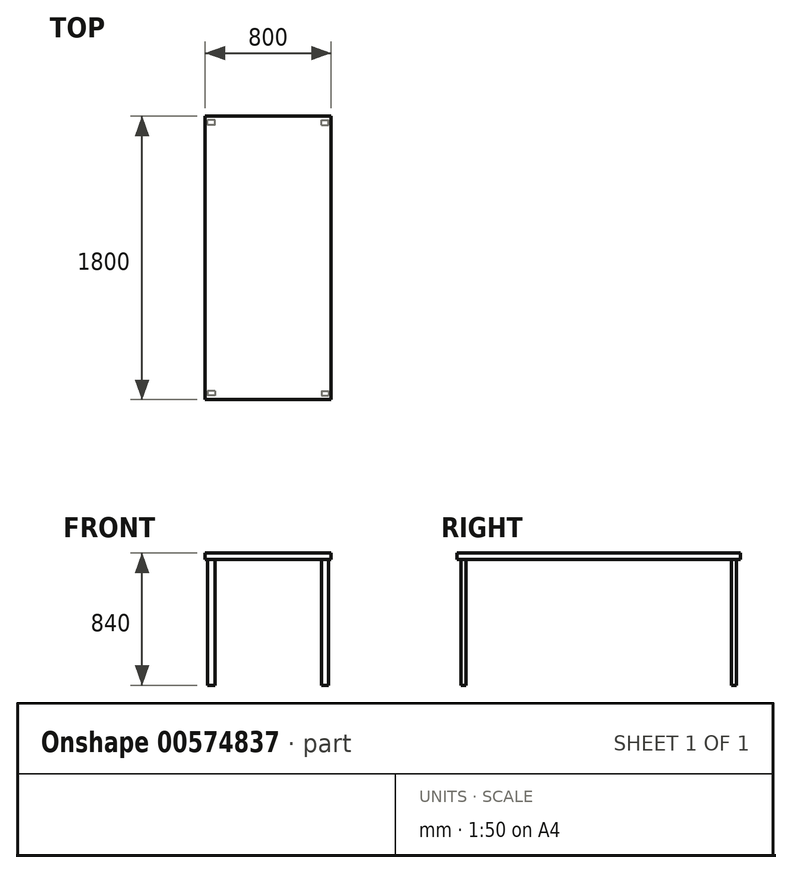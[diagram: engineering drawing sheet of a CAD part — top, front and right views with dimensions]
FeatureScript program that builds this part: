
annotation { "Feature Type Name" : "Feature", "Feature Type Description" : "" }
export const myFeature = defineFeature(function(context is Context, id is Id, definition is map)
    precondition{}
    {
        {
            var Q0;
            Q0=qCreatedBy(makeId("Front.planeOp"),FACE);
            var sketch = newSketch(context, id + "F0", { "sketchPlane" : qUnion([Q0])});
            skLineSegment(sketch, "E0.bottom", {"start": v(400, 20) * mm, "end": v(-400, 20) * mm});
            skLineSegment(sketch, "E0.top", {"start": v(400, -20) * mm, "end": v(-400, -20) * mm});
            skLineSegment(sketch, "E0.left", {"start": v(400, 20) * mm, "end": v(400, -20) * mm});
            skLineSegment(sketch, "E0.right", {"start": v(-400, 20) * mm, "end": v(-400, -20) * mm});
            skPoint(sketch, "E0.middle", {"position": v(0, 0) * mm});
            skSolve(sketch);
        }
        {
            var Q0;
            Q0 = qSketchRegion(id + "F0", true);
            extrude(context, id + "F1", {"entities" : qUnion([Q0]), "depth" : 1800 * mm, "offsetDistance" : 25.4 * mm});
        }
        {
            var Q0;
            Q0=makeQuery(id+"F1.opExtrude","SWEPT_FACE",FACE,{"disambiguationData":[OSD([sQuery(id+"F0.wireOp",EDGE,"E0.top")])]});
            var sketch = newSketch(context, id + "F2", { "sketchPlane" : qUnion([Q0])});
            skLineSegment(sketch, "E1.bottom", {"start": v(-338.59, 1744.2) * mm, "end": v(-385.13, 1744.2) * mm});
            skLineSegment(sketch, "E1.top", {"start": v(-338.59, 1774.64) * mm, "end": v(-385.13, 1774.64) * mm});
            skLineSegment(sketch, "E1.left", {"start": v(-338.59, 1744.2) * mm, "end": v(-338.59, 1774.64) * mm});
            skLineSegment(sketch, "E1.right", {"start": v(-385.13, 1744.2) * mm, "end": v(-385.13, 1774.64) * mm});
            skPoint(sketch, "E1.middle", {"position": v(-361.86, 1759.42) * mm});
            skLineSegment(sketch, "E2", {"start": v(-400, 900) * mm, "end": v(400, 900) * mm});
            skLineSegment(sketch, "E3", {"start": v(0, 1800) * mm, "end": v(0, 0) * mm});
            skLineSegment(sketch, "E4.MirrorCS", {"start": v(338.59, 1744.2) * mm, "end": v(385.13, 1744.2) * mm});
            skLineSegment(sketch, "E5.MirrorCS", {"start": v(338.59, 1744.2) * mm, "end": v(338.59, 1774.64) * mm});
            skLineSegment(sketch, "E6.MirrorCS", {"start": v(338.59, 1774.64) * mm, "end": v(385.13, 1774.64) * mm});
            skLineSegment(sketch, "E7.MirrorCS", {"start": v(385.13, 1744.2) * mm, "end": v(385.13, 1774.64) * mm});
            skPoint(sketch, "E8.MirrorP", {"position": v(361.86, 1759.42) * mm});
            skPoint(sketch, "E9.MirrorP", {"position": v(361.86, 40.58) * mm});
            skLineSegment(sketch, "E10.MirrorCS", {"start": v(338.59, 25.36) * mm, "end": v(385.13, 25.36) * mm});
            skLineSegment(sketch, "E11.MirrorCS", {"start": v(338.59, 55.8) * mm, "end": v(338.59, 25.36) * mm});
            skLineSegment(sketch, "E12.MirrorCS", {"start": v(338.59, 55.8) * mm, "end": v(385.13, 55.8) * mm});
            skLineSegment(sketch, "E13.MirrorCS", {"start": v(385.13, 55.8) * mm, "end": v(385.13, 25.36) * mm});
            skPoint(sketch, "E14.MirrorP", {"position": v(-361.86, 40.58) * mm});
            skLineSegment(sketch, "E15.MirrorCS", {"start": v(-338.59, 55.8) * mm, "end": v(-338.59, 25.36) * mm});
            skLineSegment(sketch, "E16.MirrorCS", {"start": v(-338.59, 25.36) * mm, "end": v(-385.13, 25.36) * mm});
            skLineSegment(sketch, "E17.MirrorCS", {"start": v(-385.13, 55.8) * mm, "end": v(-385.13, 25.36) * mm});
            skLineSegment(sketch, "E18.MirrorCS", {"start": v(-338.59, 55.8) * mm, "end": v(-385.13, 55.8) * mm});
            skSolve(sketch);
        }
        {
            var Q0;
            Q0 = qSketchRegion(id + "F2", true);
            extrude(context, id + "F3", {"entities" : qUnion([Q0]), "operationType" : NewBodyOperationType.ADD, "depth" : 800 * mm, "offsetDistance" : 25.4 * mm});
        }
    });
